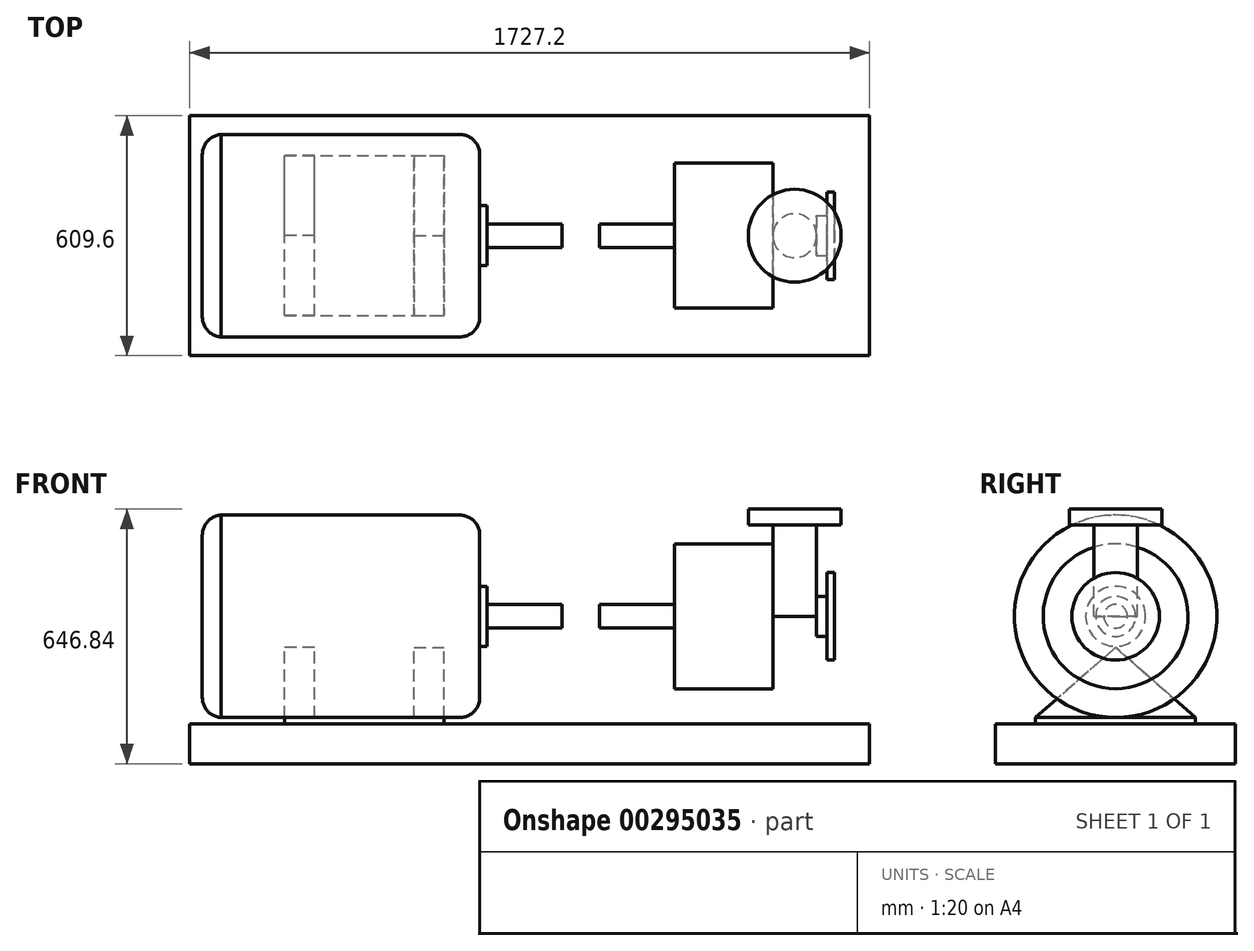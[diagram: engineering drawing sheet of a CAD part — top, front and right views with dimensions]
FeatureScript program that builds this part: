
annotation { "Feature Type Name" : "Feature", "Feature Type Description" : "" }
export const myFeature = defineFeature(function(context is Context, id is Id, definition is map)
    precondition{}
    {
        {
            var Q0;
            Q0=qCreatedBy(makeId("Front.planeOp"),FACE);
            var sketch = newSketch(context, id + "F0", { "sketchPlane" : qUnion([Q0])});
            skLineSegment(sketch, "E0.bottom", {"start": v(-863.6, -50.8) * mm, "end": v(863.6, -50.8) * mm});
            skLineSegment(sketch, "E0.top", {"start": v(-863.6, 50.8) * mm, "end": v(863.6, 50.8) * mm});
            skLineSegment(sketch, "E0.left", {"start": v(-863.6, -50.8) * mm, "end": v(-863.6, 50.8) * mm});
            skLineSegment(sketch, "E0.right", {"start": v(863.6, -50.8) * mm, "end": v(863.6, 50.8) * mm});
            skPoint(sketch, "E0.middle", {"position": v(0, 0) * mm});
            skLineSegment(sketch, "E1", {"start": v(-863.6, 50.8) * mm, "end": v(-736.6, 50.8) * mm});
            skLineSegment(sketch, "E2", {"start": v(-736.6, 50.8) * mm, "end": v(-533.4, 50.8) * mm});
            skLineSegment(sketch, "E3", {"start": v(-831.85, 581.1) * mm, "end": v(82.55, 581.1) * mm});
            skLineSegment(sketch, "E4.bottom", {"start": v(82.55, 293.69) * mm, "end": v(82.55, 293.69) * mm});
            skLineSegment(sketch, "E4.top", {"start": v(82.55, 354.01) * mm, "end": v(82.55, 354.01) * mm});
            skLineSegment(sketch, "E4.left", {"start": v(82.55, 293.69) * mm, "end": v(82.55, 354.01) * mm});
            skLineSegment(sketch, "E4.right", {"start": v(82.55, 293.69) * mm, "end": v(82.55, 354.01) * mm});
            skPoint(sketch, "E4.middle", {"position": v(82.55, 323.85) * mm});
            skLineSegment(sketch, "E5", {"start": v(82.55, 293.69) * mm, "end": v(-107.95, 293.69) * mm});
            skLineSegment(sketch, "E6", {"start": v(-107.95, 293.69) * mm, "end": v(-107.95, 354.01) * mm});
            skLineSegment(sketch, "E7", {"start": v(-107.95, 354.01) * mm, "end": v(82.55, 354.01) * mm});
            skLineSegment(sketch, "E8.bottom", {"start": v(-107.95, 400.05) * mm, "end": v(-127, 400.05) * mm});
            skLineSegment(sketch, "E8.top", {"start": v(-107.95, 247.65) * mm, "end": v(-127, 247.65) * mm});
            skLineSegment(sketch, "E8.left", {"start": v(-107.95, 400.05) * mm, "end": v(-107.95, 247.65) * mm});
            skLineSegment(sketch, "E8.right", {"start": v(-127, 400.05) * mm, "end": v(-127, 247.65) * mm});
            skLineSegment(sketch, "E9.bottom", {"start": v(-234.3, 66.68) * mm, "end": v(-127, 66.68) * mm});
            skLineSegment(sketch, "E9.top", {"start": v(-234.3, 581.03) * mm, "end": v(-127, 581.03) * mm});
            skLineSegment(sketch, "E9.left", {"start": v(-234.3, 66.68) * mm, "end": v(-234.3, 581.03) * mm});
            skLineSegment(sketch, "E9.right", {"start": v(-127, 66.68) * mm, "end": v(-127, 581.03) * mm});
            skPoint(sketch, "E9.middle", {"position": v(-180.65, 323.85) * mm});
            skLineSegment(sketch, "E10", {"start": v(-234.3, 66.68) * mm, "end": v(-831.85, 66.68) * mm});
            skLineSegment(sketch, "E11", {"start": v(-831.85, 66.68) * mm, "end": v(-831.85, 581.1) * mm});
            skLineSegment(sketch, "E12", {"start": v(-831.85, 581.1) * mm, "end": v(-781.05, 581.1) * mm});
            skLineSegment(sketch, "E13", {"start": v(-781.05, 581.1) * mm, "end": v(-781.05, 530.3) * mm});
            skLineSegment(sketch, "E14", {"start": v(82.55, 323.85) * mm, "end": v(-831.85, 323.85) * mm});
            skArc(sketch, "E15", {"start": v(-781.05, 581.1) * mm, "mid": v(-816.97, 566.22) * mm, "end": v(-831.85, 530.3) * mm});
            skLineSegment(sketch, "E16", {"start": v(-127, 581.03) * mm, "end": v(-177.8, 581.03) * mm});
            skLineSegment(sketch, "E17", {"start": v(-177.8, 581.03) * mm, "end": v(-177.8, 530.23) * mm});
            skArc(sketch, "E18", {"start": v(-177.8, 581.03) * mm, "mid": v(-141.88, 566.15) * mm, "end": v(-127, 530.23) * mm});
            skArc(sketch, "E19.MirrorCS", {"start": v(-781.05, 66.6) * mm, "mid": v(-816.97, 81.48) * mm, "end": v(-831.85, 117.4) * mm});
            skArc(sketch, "E20.MirrorCS", {"start": v(-177.8, 66.67) * mm, "mid": v(-141.88, 81.55) * mm, "end": v(-127, 117.47) * mm});
            skLineSegment(sketch, "E21", {"start": v(-831.85, 66.68) * mm, "end": v(-831.85, 50.8) * mm});
            skLineSegment(sketch, "E22", {"start": v(-127, 66.68) * mm, "end": v(-127, 50.8) * mm});
            skLineSegment(sketch, "E23", {"start": v(-217.28, 66.68) * mm, "end": v(-217.28, 50.8) * mm});
            skLineSegment(sketch, "E24", {"start": v(-623.08, 66.68) * mm, "end": v(-623.08, 50.8) * mm});
            skLineSegment(sketch, "E25", {"start": v(82.55, 323.85) * mm, "end": v(774.7, 323.85) * mm});
            skLineSegment(sketch, "E26", {"start": v(774.7, 323.85) * mm, "end": v(774.7, 435.1) * mm});
            skLineSegment(sketch, "E27", {"start": v(774.7, 435.1) * mm, "end": v(755.65, 435.1) * mm});
            skLineSegment(sketch, "E28", {"start": v(755.65, 435.1) * mm, "end": v(755.65, 212.6) * mm});
            skLineSegment(sketch, "E29", {"start": v(755.65, 212.6) * mm, "end": v(774.7, 212.6) * mm});
            skLineSegment(sketch, "E30", {"start": v(774.7, 212.6) * mm, "end": v(774.7, 323.85) * mm});
            skLineSegment(sketch, "E31", {"start": v(774.7, 323.85) * mm, "end": v(673.1, 323.85) * mm});
            skLineSegment(sketch, "E32", {"start": v(673.1, 323.85) * mm, "end": v(728.73, 323.85) * mm});
            skLineSegment(sketch, "E33", {"start": v(728.73, 323.85) * mm, "end": v(728.73, 374.65) * mm});
            skLineSegment(sketch, "E34", {"start": v(728.73, 374.65) * mm, "end": v(755.65, 374.65) * mm});
            skLineSegment(sketch, "E35", {"start": v(728.73, 323.85) * mm, "end": v(728.73, 555.5) * mm});
            skLineSegment(sketch, "E36", {"start": v(728.73, 555.5) * mm, "end": v(673.1, 555.5) * mm});
            skLineSegment(sketch, "E37", {"start": v(673.1, 555.5) * mm, "end": v(617.47, 555.5) * mm});
            skLineSegment(sketch, "E38", {"start": v(673.1, 555.5) * mm, "end": v(673.1, 323.85) * mm});
            skLineSegment(sketch, "E39", {"start": v(728.73, 323.85) * mm, "end": v(728.73, 139.7) * mm});
            skLineSegment(sketch, "E40", {"start": v(774.7, 323.85) * mm, "end": v(177.8, 323.85) * mm});
            skLineSegment(sketch, "E41.MirrorCS", {"start": v(728.73, 273.05) * mm, "end": v(755.65, 273.05) * mm});
            skLineSegment(sketch, "E42", {"start": v(617.47, 555.5) * mm, "end": v(617.47, 323.85) * mm});
            skLineSegment(sketch, "E43", {"start": v(617.47, 555.5) * mm, "end": v(555.04, 555.5) * mm});
            skLineSegment(sketch, "E44", {"start": v(555.04, 555.5) * mm, "end": v(555.04, 596.04) * mm});
            skLineSegment(sketch, "E45", {"start": v(555.04, 596.04) * mm, "end": v(812, 596.04) * mm});
            skLineSegment(sketch, "E46", {"start": v(812, 596.04) * mm, "end": v(812, 555.5) * mm});
            skLineSegment(sketch, "E47", {"start": v(812, 555.5) * mm, "end": v(728.73, 555.5) * mm});
            skLineSegment(sketch, "E48", {"start": v(177.8, 323.85) * mm, "end": v(177.8, 354.01) * mm});
            skLineSegment(sketch, "E49", {"start": v(177.8, 354.01) * mm, "end": v(177.8, 293.69) * mm});
            skLineSegment(sketch, "E50", {"start": v(177.8, 293.69) * mm, "end": v(368.3, 293.69) * mm});
            skLineSegment(sketch, "E51", {"start": v(177.8, 354.01) * mm, "end": v(368.3, 354.01) * mm});
            skLineSegment(sketch, "E52", {"start": v(368.3, 354.01) * mm, "end": v(368.3, 293.69) * mm});
            skLineSegment(sketch, "E53", {"start": v(728.73, 139.7) * mm, "end": v(368.3, 139.7) * mm});
            skLineSegment(sketch, "E54", {"start": v(368.3, 139.7) * mm, "end": v(368.3, 293.69) * mm});
            skLineSegment(sketch, "E55", {"start": v(368.3, 323.85) * mm, "end": v(368.3, 508) * mm});
            skLineSegment(sketch, "E56", {"start": v(368.3, 508) * mm, "end": v(728.73, 508) * mm});
            skLineSegment(sketch, "E57", {"start": v(689.5, 139.7) * mm, "end": v(705.28, 50.8) * mm});
            skLineSegment(sketch, "E58", {"start": v(705.28, 50.8) * mm, "end": v(588.1, 50.8) * mm});
            skLineSegment(sketch, "E59", {"start": v(588.1, 50.8) * mm, "end": v(615.14, 139.7) * mm});
            skLineSegment(sketch, "E60", {"start": v(394.3, 139.7) * mm, "end": v(368.3, 50.8) * mm});
            skLineSegment(sketch, "E61", {"start": v(368.3, 50.8) * mm, "end": v(455.14, 50.8) * mm});
            skLineSegment(sketch, "E62", {"start": v(455.14, 50.8) * mm, "end": v(455.14, 139.7) * mm});
            skLineSegment(sketch, "E63", {"start": v(673.1, 555.5) * mm, "end": v(673.1, 596.04) * mm});
            skSolve(sketch);
        }
        {
            var Q0;
            {var subQ0=sQuery(id+"F0.wireOp",EDGE,"E14");var subQ1=sQuery(id+"F0.wireOp",EDGE,"E11");var subQ2=makeQuery(id+"F0.imprint","INTERSECT",VERTEX,{"derivedFrom":[subQ1,subQ0]});Q0=makeQuery(id+"F0.imprint","IMPRINT",FACE,{"disambiguationData":[TD([[makeQuery(id+"F0.imprint","IMPRINT",EDGE,{"disambiguationData":[TD([[subQ2,1.0]])],"derivedFrom":subQ1}),-1.0]])]});}
            var Q1;
            {var subQ4=sQuery(id+"F0.wireOp",EDGE,"E20.MirrorCS");Q1=makeQuery(id+"F0.imprint","IMPRINT",FACE,{"disambiguationData":[TD([[makeQuery(id+"F0.imprint","IMPRINT",EDGE,{"derivedFrom":subQ4}),1.0]])]});}
            var Q2;
            {var subQ1=sQuery(id+"F0.wireOp",EDGE,"E8.top");Q2=makeQuery(id+"F0.imprint","IMPRINT",FACE,{"disambiguationData":[TD([[makeQuery(id+"F0.imprint","IMPRINT",EDGE,{"derivedFrom":subQ1}),-1.0]])]});}
            var Q3;
            {var subQ0=sQuery(id+"F0.wireOp",EDGE,"E5");Q3=makeQuery(id+"F0.imprint","IMPRINT",FACE,{"disambiguationData":[TD([[makeQuery(id+"F0.imprint","IMPRINT",EDGE,{"derivedFrom":subQ0}),-1.0]])]});}
            var Q4;
            Q4=sQuery(id+"F0.wireOp",EDGE,"E14");
            revolve(context, id + "F1", {"entities" : qUnion([Q0, Q1, Q2, Q3]), "axis" : qUnion([Q4]), "revolveType" : RevolveType.FULL});
        }
        {
            var Q0;
            {var subQ4=sQuery(id+"F0.wireOp",EDGE,"E23");Q0=makeQuery(id+"F0.imprint","IMPRINT",FACE,{"disambiguationData":[TD([[makeQuery(id+"F0.imprint","IMPRINT",EDGE,{"derivedFrom":subQ4}),-1.0]])]});}
            extrude(context, id + "F2", {"entities" : qUnion([Q0]), "operationType" : NewBodyOperationType.ADD, "endBound" : BoundingType.SYMMETRIC, "depth" : 406.4 * mm});
        }
        {
            var Q0;
            Q0=makeQuery(id+"F2.opExtrude","SWEPT_FACE",FACE,{"disambiguationData":[OSD([sQuery(id+"F0.wireOp",EDGE,"E24")])]});
            var sketch = newSketch(context, id + "F3", { "sketchPlane" : qUnion([Q0])});
            skLineSegment(sketch, "E64", {"start": v(0, 66.68) * mm, "end": v(0, 244.48) * mm});
            skPoint(sketch, "E64.endSnap0", {"position": v(0, 66.68) * mm});
            skLineSegment(sketch, "E65", {"start": v(0, 244.48) * mm, "end": v(-203.2, 66.68) * mm});
            skLineSegment(sketch, "E66", {"start": v(-203.2, 66.68) * mm, "end": v(203.2, 66.68) * mm});
            skLineSegment(sketch, "E67", {"start": v(203.2, 66.68) * mm, "end": v(0, 244.48) * mm});
            skSolve(sketch);
        }
        {
            var Q0;
            {var subQ0=sQuery(id+"F3.wireOp",EDGE,"E64");Q0=makeQuery(id+"F3.imprint","IMPRINT",FACE,{"disambiguationData":[TD([[makeQuery(id+"F3.imprint","IMPRINT",EDGE,{"derivedFrom":subQ0}),-1.0]])]});}
            var Q1;
            {var subQ0=sQuery(id+"F3.wireOp",EDGE,"E64");Q1=makeQuery(id+"F3.imprint","IMPRINT",FACE,{"disambiguationData":[TD([[makeQuery(id+"F3.imprint","IMPRINT",EDGE,{"derivedFrom":subQ0}),1.0]])]});}
            extrude(context, id + "F4", {"entities" : qUnion([Q0, Q1]), "oppositeDirection" : true, "depth" : 76.2 * mm});
        }
        {
            var Q0;
            Q0=makeQuery(id+"F2.opExtrude","SWEPT_FACE",FACE,{"disambiguationData":[OSD([sQuery(id+"F0.wireOp",EDGE,"E23")])]});
            var sketch = newSketch(context, id + "F5", { "sketchPlane" : qUnion([Q0])});
            skLineSegment(sketch, "E68", {"start": v(0, 66.68) * mm, "end": v(0, 244.48) * mm});
            skPoint(sketch, "E68.endSnap0", {"position": v(0, 66.68) * mm});
            skLineSegment(sketch, "E69", {"start": v(0, 244.48) * mm, "end": v(-203.2, 66.68) * mm});
            skLineSegment(sketch, "E70", {"start": v(-203.2, 66.68) * mm, "end": v(203.2, 66.68) * mm});
            skLineSegment(sketch, "E71", {"start": v(203.2, 66.68) * mm, "end": v(0, 244.48) * mm});
            skSolve(sketch);
        }
        {
            var Q0;
            {var subQ0=sQuery(id+"F5.wireOp",EDGE,"E68");Q0=makeQuery(id+"F5.imprint","IMPRINT",FACE,{"disambiguationData":[TD([[makeQuery(id+"F5.imprint","IMPRINT",EDGE,{"derivedFrom":subQ0}),1.0]])]});}
            var Q1;
            {var subQ0=sQuery(id+"F5.wireOp",EDGE,"E68");Q1=makeQuery(id+"F5.imprint","IMPRINT",FACE,{"disambiguationData":[TD([[makeQuery(id+"F5.imprint","IMPRINT",EDGE,{"derivedFrom":subQ0}),-1.0]])]});}
            extrude(context, id + "F6", {"entities" : qUnion([Q0, Q1]), "oppositeDirection" : true, "depth" : 76.2 * mm});
        }
        {
            var Q0;
            Q0=makeQuery(id+"F0.imprint","IMPRINT",FACE,{"disambiguationData":[TD([[makeQuery(id+"F0.imprint","IMPRINT",EDGE,{"derivedFrom":sQuery(id+"F0.wireOp",EDGE,"E0.bottom")}),1.0]])]});
            extrude(context, id + "F7", {"entities" : qUnion([Q0]), "operationType" : NewBodyOperationType.ADD, "endBound" : BoundingType.SYMMETRIC, "depth" : 609.6 * mm});
        }
        {
            var Q0;
            {var subQ4=sQuery(id+"F0.wireOp",EDGE,"E50");Q0=makeQuery(id+"F0.imprint","IMPRINT",FACE,{"disambiguationData":[TD([[makeQuery(id+"F0.imprint","IMPRINT",EDGE,{"derivedFrom":subQ4}),1.0]])]});}
            var Q1;
            {var subQ7=sQuery(id+"F0.wireOp",EDGE,"E52");Q1=makeQuery(id+"F0.imprint","IMPRINT",FACE,{"disambiguationData":[TD([[makeQuery(id+"F0.imprint","IMPRINT",EDGE,{"derivedFrom":subQ7}),1.0]])]});}
            var Q2;
            {var subQ0=sQuery(id+"F0.wireOp",EDGE,"E41.MirrorCS");Q2=makeQuery(id+"F0.imprint","IMPRINT",FACE,{"disambiguationData":[TD([[makeQuery(id+"F0.imprint","IMPRINT",EDGE,{"derivedFrom":subQ0}),1.0]])]});}
            var Q3;
            {var subQ4=sQuery(id+"F0.wireOp",EDGE,"E29");Q3=makeQuery(id+"F0.imprint","IMPRINT",FACE,{"disambiguationData":[TD([[makeQuery(id+"F0.imprint","IMPRINT",EDGE,{"derivedFrom":subQ4}),1.0]])]});}
            var Q4;
            Q4=sQuery(id+"F0.wireOp",EDGE,"E40");
            revolve(context, id + "F8", {"entities" : qUnion([Q0, Q1, Q2, Q3]), "axis" : qUnion([Q4]), "revolveType" : RevolveType.FULL});
        }
        {
            var Q0;
            Q0=makeQuery(id+"F0.imprint","IMPRINT",FACE,{"disambiguationData":[TD([[makeQuery(id+"F0.imprint","IMPRINT",EDGE,{"derivedFrom":sQuery(id+"F0.wireOp",EDGE,"E37")}),-1.0]])]});
            var Q1;
            {var subQ0=sQuery(id+"F0.wireOp",EDGE,"E37");Q1=makeQuery(id+"F0.imprint","IMPRINT",FACE,{"disambiguationData":[TD([[makeQuery(id+"F0.imprint","IMPRINT",EDGE,{"derivedFrom":subQ0}),1.0]])]});}
            var Q2;
            {var subQ0=sQuery(id+"F0.wireOp",EDGE,"E40");var subQ1=sQuery(id+"F0.wireOp",EDGE,"E38");var subQ2=makeQuery(id+"F0.imprint","INTERSECT",VERTEX,{"derivedFrom":[subQ1,subQ0]});Q2=makeQuery(id+"F0.imprint","IMPRINT",FACE,{"disambiguationData":[TD([[makeQuery(id+"F0.imprint","IMPRINT",EDGE,{"disambiguationData":[TD([[subQ2,1.0]])],"derivedFrom":subQ1}),-1.0]])]});}
            var Q3;
            Q3=sQuery(id+"F0.wireOp",EDGE,"E38");
            revolve(context, id + "F9", {"entities" : qUnion([Q0, Q1, Q2]), "axis" : qUnion([Q3]), "revolveType" : RevolveType.FULL});
        }
    });
